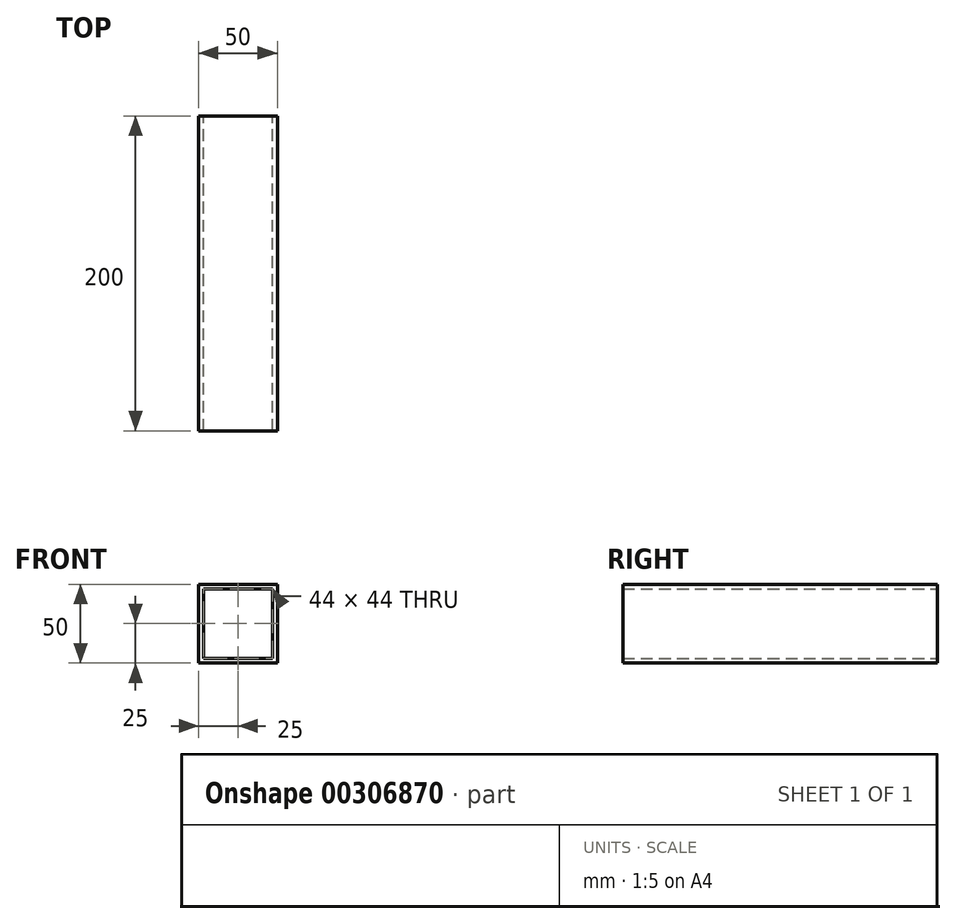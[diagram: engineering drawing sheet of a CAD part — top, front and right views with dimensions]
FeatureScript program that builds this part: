
annotation { "Feature Type Name" : "Feature", "Feature Type Description" : "" }
export const myFeature = defineFeature(function(context is Context, id is Id, definition is map)
    precondition{}
    {
        {
            var Q0;
            Q0=qCreatedBy(makeId("Front.planeOp"),FACE);
            var sketch = newSketch(context, id + "F0", { "sketchPlane" : qUnion([Q0])});
            skLineSegment(sketch, "E0.bottom", {"start": v(0, 0) * mm, "end": v(50, 0) * mm});
            skLineSegment(sketch, "E0.top", {"start": v(0, 50) * mm, "end": v(50, 50) * mm});
            skLineSegment(sketch, "E0.left", {"start": v(0, 0) * mm, "end": v(0, 50) * mm});
            skLineSegment(sketch, "E0.right", {"start": v(50, 0) * mm, "end": v(50, 50) * mm});
            skLineSegment(sketch, "E1.0", {"start": v(3, 3) * mm, "end": v(3, 47) * mm});
            skLineSegment(sketch, "E1.1", {"start": v(3, 3) * mm, "end": v(47, 3) * mm});
            skLineSegment(sketch, "E1.2", {"start": v(47, 3) * mm, "end": v(47, 47) * mm});
            skLineSegment(sketch, "E1.3", {"start": v(3, 47) * mm, "end": v(47, 47) * mm});
            skSolve(sketch);
        }
        {
            var Q0;
            Q0=makeQuery(id+"F0.imprint","IMPRINT",FACE,{"disambiguationData":[TD([[makeQuery(id+"F0.imprint","IMPRINT",EDGE,{"derivedFrom":sQuery(id+"F0.wireOp",EDGE,"E0.bottom")}),1.0]])]});
            extrude(context, id + "F1", {"entities" : qUnion([Q0]), "depth" : 200 * mm});
        }
    });
